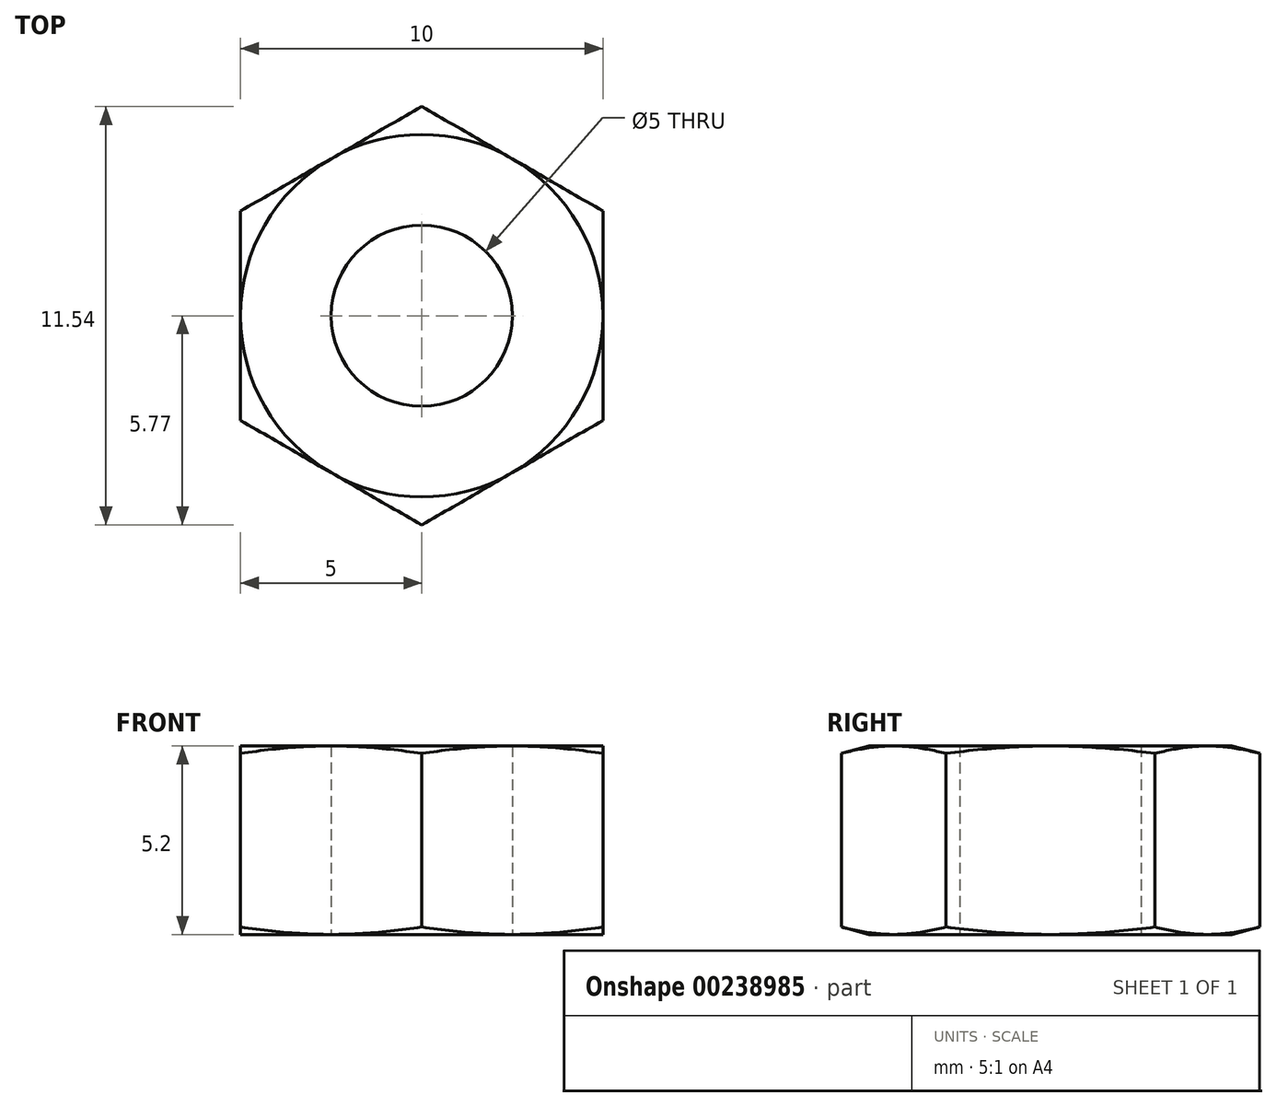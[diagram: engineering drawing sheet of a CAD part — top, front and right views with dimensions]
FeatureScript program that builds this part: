
annotation { "Feature Type Name" : "Feature", "Feature Type Description" : "" }
export const myFeature = defineFeature(function(context is Context, id is Id, definition is map)
    precondition{}
    {
        {
            var Q0;
            Q0=qCreatedBy(makeId("Top.planeOp"),FACE);
            var sketch = newSketch(context, id + "F0", { "sketchPlane" : qUnion([Q0])});
            skCircle(sketch, "E0.cCircle", {"center": v(0, 0) * mm, "radius": 5 * mm, "construction": true});
            skLineSegment(sketch, "E0.0", {"start": v(5, 2.89) * mm, "end": v(5, -2.89) * mm});
            skLineSegment(sketch, "E0.1", {"start": v(5, -2.89) * mm, "end": v(0, -5.77) * mm});
            skLineSegment(sketch, "E0.2", {"start": v(0, -5.77) * mm, "end": v(-5, -2.89) * mm});
            skLineSegment(sketch, "E0.3", {"start": v(-5, -2.89) * mm, "end": v(-5, 2.89) * mm});
            skLineSegment(sketch, "E0.4", {"start": v(-5, 2.89) * mm, "end": v(0, 5.77) * mm});
            skLineSegment(sketch, "E0.5", {"start": v(0, 5.77) * mm, "end": v(5, 2.89) * mm});
            skPoint(sketch, "E0.0.midPoint", {"position": v(5, 0) * mm});
            skCircle(sketch, "E1", {"center": v(0, 0) * mm, "radius": 2.5 * mm});
            skLineSegment(sketch, "E2", {"start": v(-12.53, -7.23) * mm, "end": v(14.01, 8.09) * mm, "construction": true});
            skPoint(sketch, "E3", {"position": v(-4.33, -2.5) * mm});
            skPoint(sketch, "E4", {"position": v(-5, -2.89) * mm});
            skSolve(sketch);
        }
        {
            var Q0;
            Q0=qSketchRegion(id+"F0",true);
            extrude(context, id + "F1", {"entities" : qUnion([Q0]), "depth" : 5.2 * mm});
        }
        {
            var Q0;
            Q0=makeQuery(id+"F1.opExtrude","SWEPT_EDGE",EDGE,{"disambiguationData":[OSD([sQuery(id+"F0.wireOp",EDGE,"E0.2"),sQuery(id+"F0.wireOp",EDGE,"E0.3")])]});
            cPoint(context, id + "F2", {"entities" : qUnion([Q0]), "parameter" : 0.5});
        }
        {
            var Q0;
            Q0=makeQuery(id+"F1.opExtrude","SWEPT_EDGE",EDGE,{"disambiguationData":[OSD([sQuery(id+"F0.wireOp",EDGE,"E0.0"),sQuery(id+"F0.wireOp",EDGE,"E0.5")])]});
            cPoint(context, id + "F3", {"entities" : qUnion([Q0]), "parameter" : 0.5});
        }
        {
            var Q0;
            Q0=qCreatedBy(id+"F2",VERTEX);
            var Q1;
            Q1=qCreatedBy(id+"F3",VERTEX);
            var Q2;
            Q2=makeQuery(id+"F1.opExtrude","CAP_VERTEX",VERTEX,{"disambiguationData":[OSD([sQuery(id+"F0.wireOp",EDGE,"E0.0"),sQuery(id+"F0.wireOp",EDGE,"E0.5")])],"isStart":true});
            cPlane(context, id + "F4", {"entities" : qUnion([Q0, Q1, Q2]), "cplaneType" : CPlaneType.THREE_POINT, "offset" : 25 * mm, "width" : 150 * mm, "height" : 150 * mm});
        }
        {
            var Q0;
            Q0=qCreatedBy(id+"F4.planeOp",FACE);
            var sketch = newSketch(context, id + "F5", { "sketchPlane" : qUnion([Q0])});
            skPoint(sketch, "E5.0", {"position": v(-5, 0) * mm});
            skLineSegment(sketch, "E6", {"start": v(-2.67, -0.62) * mm, "end": v(-10.4, 1.45) * mm});
            skPoint(sketch, "E7", {"position": v(-5.77, 5.2) * mm});
            skPoint(sketch, "E8", {"position": v(-5.77, 2.6) * mm});
            skLineSegment(sketch, "E9", {"start": v(-9.86, 2.6) * mm, "end": v(11.5, 2.6) * mm, "construction": true});
            skLineSegment(sketch, "E10", {"start": v(-10.4, -0.62) * mm, "end": v(-2.67, -0.62) * mm});
            skLineSegment(sketch, "E11", {"start": v(-10.4, 1.45) * mm, "end": v(-10.4, -0.62) * mm});
            skLineSegment(sketch, "E12", {"start": v(0, -0.96) * mm, "end": v(0, 9.49) * mm, "construction": true});
            skLineSegment(sketch, "E13.MirrorCS", {"start": v(-2.67, 5.82) * mm, "end": v(-10.4, 3.75) * mm});
            skLineSegment(sketch, "E14.MirrorCS", {"start": v(-10.4, 3.75) * mm, "end": v(-10.4, 5.83) * mm});
            skLineSegment(sketch, "E15.MirrorCS", {"start": v(-10.4, 5.83) * mm, "end": v(-2.67, 5.83) * mm});
            skPoint(sketch, "E16.orphan", {"position": v(-2.89, 0) * mm});
            skPoint(sketch, "E17.trimOffspring.end.orphan", {"position": v(-5.77, 0) * mm});
            skLineSegment(sketch, "E18.0", {"start": v(-2.89, 5.2) * mm, "end": v(-5.77, 5.2) * mm});
            skSolve(sketch);
        }
        {
            var Q0;
            Q0=makeQuery(id+"F5.imprint","IMPRINT",FACE,{"disambiguationData":[TD([[makeQuery(id+"F5.imprint","IMPRINT",EDGE,{"derivedFrom":sQuery(id+"F5.wireOp",EDGE,"E13.MirrorCS")}),-1.0]])]});
            var Q1;
            Q1=makeQuery(id+"F5.imprint","IMPRINT",FACE,{"disambiguationData":[TD([[makeQuery(id+"F5.imprint","IMPRINT",EDGE,{"derivedFrom":sQuery(id+"F5.wireOp",EDGE,"E6")}),1.0]])]});
            var Q2;
            Q2=sQuery(id+"F5.wireOp",EDGE,"E12");
            revolve(context, id + "F6", {"operationType" : NewBodyOperationType.REMOVE, "entities" : qUnion([Q0, Q1]), "axis" : qUnion([Q2]), "revolveType" : RevolveType.FULL, "oppositeDirection" : true});
        }
    });
